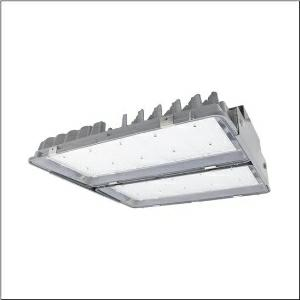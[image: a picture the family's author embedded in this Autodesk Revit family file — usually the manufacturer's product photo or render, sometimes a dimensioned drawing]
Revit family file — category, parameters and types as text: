
# Revit family: highbay_11xtreme_51hf62db4tma
name_source: partatom
category: Lighting Fixtures
units: mm (PartAtom-declared; Revit-internal decimal feet)

## family parameters
Cut with Voids When Loaded = No
Host = Face
Light Source = No
Part Type = Normal
Room Calculation Point = No
Round Connector Dimension = Use Diameter
Shared = No

## types (1)
- --- (1 x LED, 54000 lm, 285.7 W, 4000K)
    Apparent Load = 286 VA
    CIE Flux Codes = 84 96 100 100 100
    Color Rendering = 80
    Color Temperature = 4000K
    Default Elevation = 1800 mm
    Description = Highbay 11Xtreme, high bay luminaire, primary light control with lens, of PMMA, primary optical cover: cover, of toughened safety glass, light emission: direct distribution, primary light characteristic: symmetric, installation type: suspended mounting, surface-mounted, 2x LED module,for 1x 2x LED, rated luminous flux: 54.000lm, luminous efficacy: 189lm/W, light colour: 840, colour temperature: 4000K, control gear: DALI 2, with cable H07RN-F 5x 1.5mm², mains connection: 220..240V, AC, 50/60Hz, cable length: 1,5m, rated input power: 286W, luminaire housing, of diecast aluminium, coated, silver, length: 595mm, width: 560mm, height: 195mm, protection rating (complete): IP66, insulation class (complete): insulation class I (protective earthing), certification: CE, ENEC, UKCA, protection symbol: D, ball protection: ball impact resistant according to DIN VDE 0710 part 13 (with chain suspension), impact resistance: IK08, permissible operating ambient temperature: -25..+60°C, reducing of maximum allowable ambient temperature of 5°C with ceiling mounting, packaging unit: 1 piece
    Height = 157 mm
    Lamp = 1 x LED
    Lamp Light Flux = 54000 lm
    Lamp Power = 285.7 W
    Lamp count = 1
    Length = 593 mm
    Luminous efficacy = 189 lm/W
    Manufacturer = Siteco
    ModVariant = No
    Model = 51HF62DB4TMA
    Mounting Place = Ceiling
    Mounting Type = Pendant
    Number of Poles = 1
    OnlyDefault = Yes
    Power Factor = 1
    Product Name = Highbay 11Xtreme
    Product group = high bay luminaire
    ProductGroupID = 902
    Protection Class = Protection class I
    Protection Degree = IP 66
    RLX_Detail_Level = 1
    RLX_Emergency_Light_Flux = 0 lm
    RLX_Emergency_Type = 0
    RLX_Emergency_Type_DB = No
    RlxData = <blob elided: 34293 chars, md5=eb8c659d>
    Socket = socket
    Standby Power = 0 W
    System Light Flux = 54000 lm
    System Power = 286 W
    Type Comments = factory setting: luminous flux: 100 % | dim-lin: 254 | 970 mA
    Type Image = l_1258340.jpg
    URL = http://relux.com
    VarID = @adj_088155
    Voltage = 0 V
    Weight = 0.00 kg
    Width = 568 mm

## geometry (parser evidence)
native form markers: Blend x4, Sweep x9
no freeform markers — native parametric forms only
